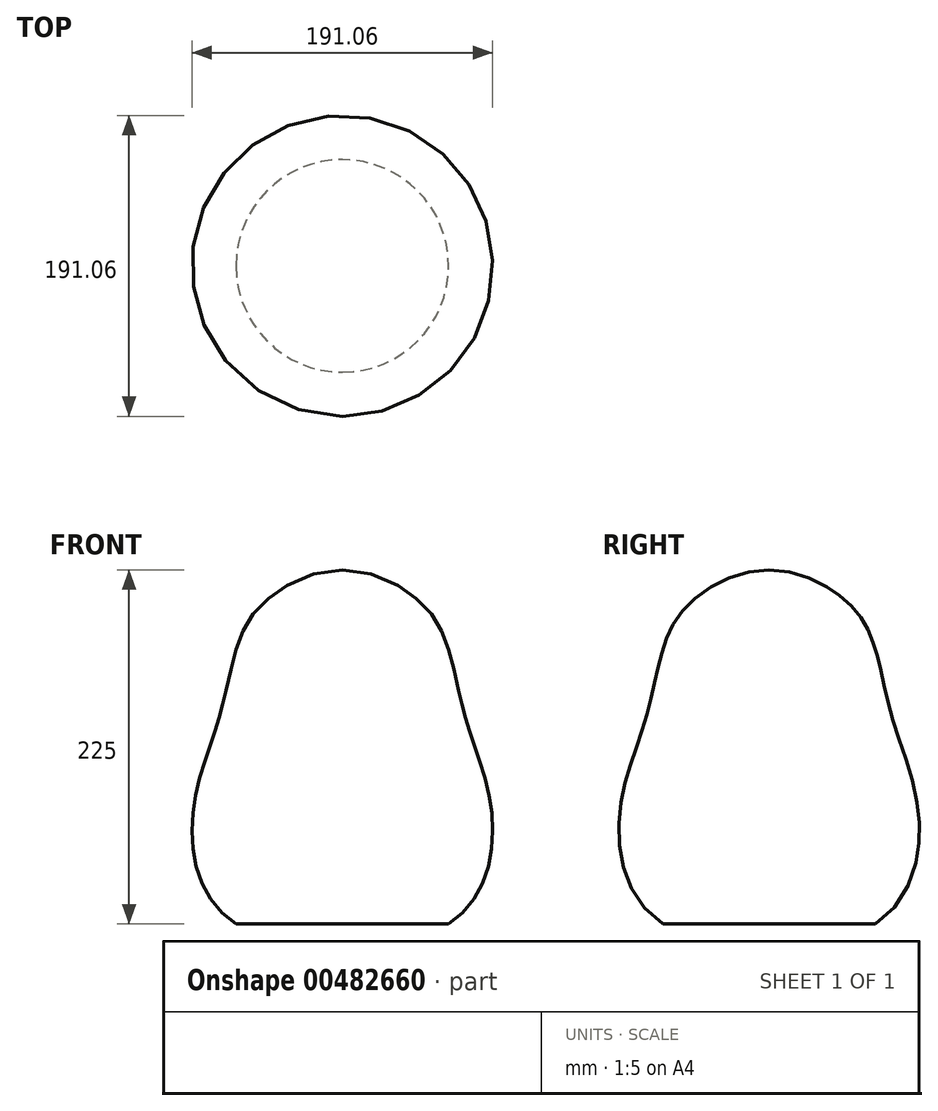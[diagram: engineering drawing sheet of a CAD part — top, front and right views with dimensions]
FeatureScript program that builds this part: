
annotation { "Feature Type Name" : "Feature", "Feature Type Description" : "" }
export const myFeature = defineFeature(function(context is Context, id is Id, definition is map)
    precondition{}
    {
        {
            var Q0;
            Q0=qCreatedBy(makeId("Right.planeOp"),FACE);
            var sketch = newSketch(context, id + "F0", { "sketchPlane" : qUnion([Q0])});
            skLineSegment(sketch, "E0", {"start": v(0, 0) * mm, "end": v(-67.5, 0) * mm});
            skLineSegment(sketch, "E1", {"start": v(0, 0) * mm, "end": v(0, 70) * mm});
            skLineSegment(sketch, "E2", {"start": v(0, 70) * mm, "end": v(-95, 70) * mm, "construction": true});
            skLineSegment(sketch, "E3", {"start": v(0, 0) * mm, "end": v(0, 125) * mm});
            skLineSegment(sketch, "E4", {"start": v(0, 125) * mm, "end": v(-80, 125) * mm, "construction": true});
            skLineSegment(sketch, "E5", {"start": v(0, 0) * mm, "end": v(0, 165) * mm});
            skLineSegment(sketch, "E6", {"start": v(0, 165) * mm, "end": v(-70, 165) * mm, "construction": true});
            skLineSegment(sketch, "E7", {"start": v(0, 0) * mm, "end": v(0, 200) * mm});
            skLineSegment(sketch, "E8", {"start": v(0, 200) * mm, "end": v(-54, 200) * mm, "construction": true});
            skLineSegment(sketch, "E9", {"start": v(0, 0) * mm, "end": v(0, 205) * mm});
            skLineSegment(sketch, "E10", {"start": v(0, 0) * mm, "end": v(0, 225) * mm});
            skLineSegment(sketch, "E11.MirrorCS", {"start": v(0, 70) * mm, "end": v(95, 70) * mm, "construction": true});
            skLineSegment(sketch, "E12.MirrorCS", {"start": v(0, 125) * mm, "end": v(80, 125) * mm, "construction": true});
            skLineSegment(sketch, "E13.MirrorCS", {"start": v(0, 165) * mm, "end": v(70, 165) * mm, "construction": true});
            skLineSegment(sketch, "E14.MirrorCS", {"start": v(0, 200) * mm, "end": v(54, 200) * mm, "construction": true});
            skLineSegment(sketch, "E15.MirrorCS", {"start": v(0, 0) * mm, "end": v(67.5, 0) * mm});
            skFitSpline(sketch, "E16", {"points": [v(-67.5, 0) * mm, v(-95, 70) * mm, v(-80, 125) * mm, v(-70, 165) * mm, v(-54, 200) * mm, v(0, 225) * mm, v(54, 200) * mm, v(70, 165) * mm, v(80, 125) * mm, v(95, 70) * mm, v(67.5, 0) * mm, v(-67.5, 0) * mm]});
            skSolve(sketch);
        }
        {
            var Q0;
            {var subQ4=sQuery(id+"F0.wireOp",EDGE,"E0");Q0=makeQuery(id+"F0.imprint","IMPRINT",FACE,{"disambiguationData":[TD([[makeQuery(id+"F0.imprint","IMPRINT",EDGE,{"derivedFrom":subQ4}),-1.0]])]});}
            var Q1;
            Q1=sQuery(id+"F0.wireOp",EDGE,"E10");
            revolve(context, id + "F1", {"entities" : qUnion([Q0]), "axis" : qUnion([Q1]), "revolveType" : RevolveType.FULL});
        }
    });
